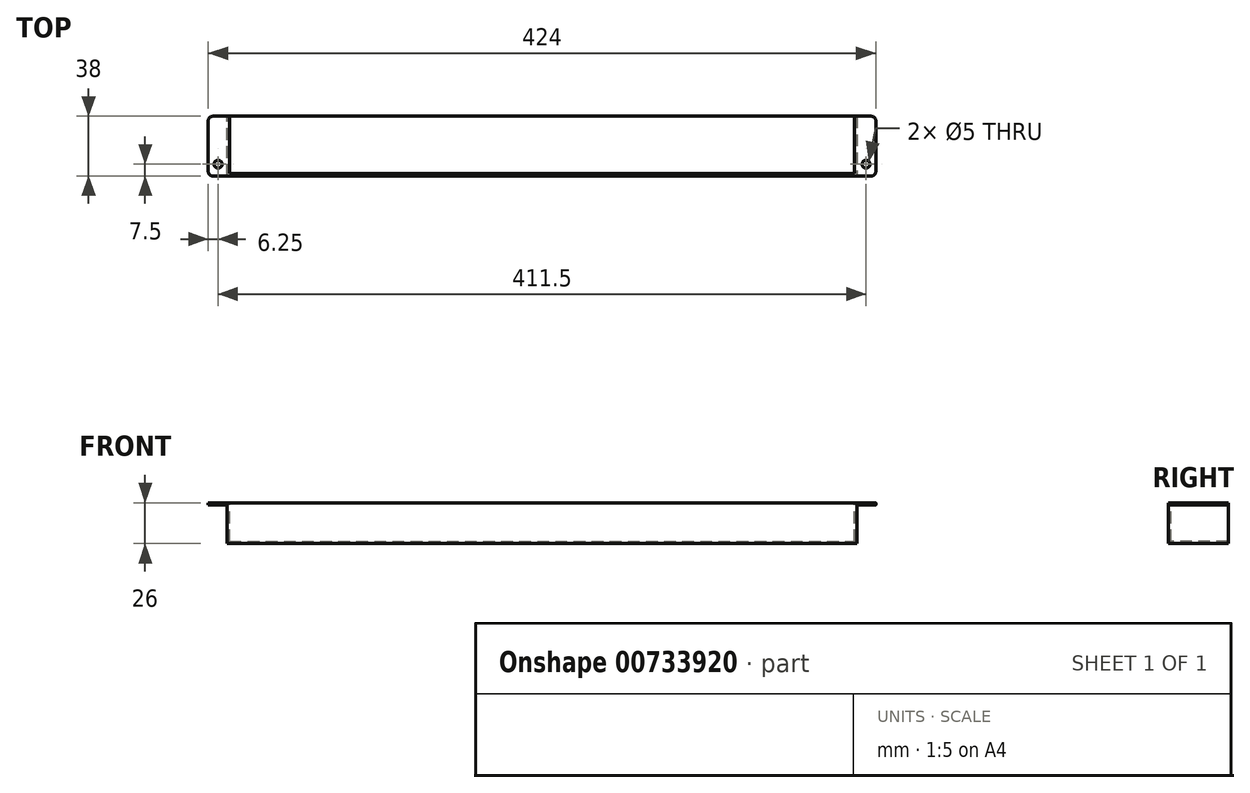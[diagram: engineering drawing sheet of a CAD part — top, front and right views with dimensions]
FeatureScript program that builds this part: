
annotation { "Feature Type Name" : "Feature", "Feature Type Description" : "" }
export const myFeature = defineFeature(function(context is Context, id is Id, definition is map)
    precondition{}
    {
        {
            var Q0;
            Q0=qCreatedBy(makeId("Front.planeOp"),FACE);
            var sketch = newSketch(context, id + "F0", { "sketchPlane" : qUnion([Q0])});
            skLineSegment(sketch, "E0.bottom", {"start": v(0, 0) * mm, "end": v(400, 0) * mm});
            skLineSegment(sketch, "E0.top", {"start": v(0, 26) * mm, "end": v(400, 26) * mm});
            skLineSegment(sketch, "E0.left", {"start": v(0, 0) * mm, "end": v(0, 26) * mm});
            skLineSegment(sketch, "E0.right", {"start": v(400, 0) * mm, "end": v(400, 26) * mm});
            skSolve(sketch);
        }
        {
            var Q0;
            Q0 = qSketchRegion(id + "F0", true);
            extrude(context, id + "F1", {"entities" : qUnion([Q0]), "oppositeDirection" : true, "depth" : 38 * mm, "offsetDistance" : 25 * mm});
        }
        {
            var Q0;
            Q0=makeQuery(id+"F1.opExtrude","SWEPT_FACE",FACE,{"disambiguationData":[OSD([sQuery(id+"F0.wireOp",EDGE,"E0.top")])]});
            var Q1;
            Q1=makeQuery(id+"F1.opExtrude","CAP_FACE",FACE,{"disambiguationData":[OSD([sQuery(id+"F0.wireOp",EDGE,"E0.bottom"),sQuery(id+"F0.wireOp",EDGE,"E0.top"),sQuery(id+"F0.wireOp",EDGE,"E0.left"),sQuery(id+"F0.wireOp",EDGE,"E0.right")])],"isStart":false});
            shell(context, id + "F2", {"entities" : qUnion([Q0, Q1]), "thickness" : 1.5 * mm});
        }
        {
            var Q0;
            Q0=makeQuery(id+"F1.opExtrude","SWEPT_FACE",FACE,{"disambiguationData":[OSD([sQuery(id+"F0.wireOp",EDGE,"E0.right")])]});
            var sketch = newSketch(context, id + "F3", { "sketchPlane" : qUnion([Q0])});
            skLineSegment(sketch, "E1.bottom", {"start": v(0, 26) * mm, "end": v(38, 26) * mm});
            skLineSegment(sketch, "E1.top", {"start": v(0, 24.5) * mm, "end": v(38, 24.5) * mm});
            skLineSegment(sketch, "E1.left", {"start": v(0, 26) * mm, "end": v(0, 24.5) * mm});
            skLineSegment(sketch, "E1.right", {"start": v(38, 26) * mm, "end": v(38, 24.5) * mm});
            skSolve(sketch);
        }
        {
            var Q0;
            Q0 = qSketchRegion(id + "F3", true);
            extrude(context, id + "F4", {"entities" : qUnion([Q0]), "operationType" : NewBodyOperationType.ADD, "depth" : 12 * mm, "offsetDistance" : 25 * mm});
        }
        {
            var Q0;
            Q0=makeQuery(id+"F1.opExtrude","SWEPT_FACE",FACE,{"disambiguationData":[OSD([sQuery(id+"F0.wireOp",EDGE,"E0.left")])]});
            var sketch = newSketch(context, id + "F5", { "sketchPlane" : qUnion([Q0])});
            skLineSegment(sketch, "E2.bottom", {"start": v(0, 26) * mm, "end": v(-38, 26) * mm});
            skLineSegment(sketch, "E2.top", {"start": v(0, 24.5) * mm, "end": v(-38, 24.5) * mm});
            skLineSegment(sketch, "E2.left", {"start": v(0, 26) * mm, "end": v(0, 24.5) * mm});
            skLineSegment(sketch, "E2.right", {"start": v(-38, 26) * mm, "end": v(-38, 24.5) * mm});
            skSolve(sketch);
        }
        {
            var Q0;
            Q0 = qSketchRegion(id + "F5", true);
            extrude(context, id + "F6", {"entities" : qUnion([Q0]), "operationType" : NewBodyOperationType.ADD, "depth" : 12 * mm, "offsetDistance" : 25 * mm});
        }
        {
            var Q0;
            Q0=makeQuery(id+"F6.boolean.opBoolean","MERGE",FACE,{"derivedFrom":[makeQuery(id+"F4.boolean.opBoolean","MERGE",FACE,{"derivedFrom":[makeQuery(id+"F1.opExtrude","SWEPT_FACE",FACE,{"disambiguationData":[OSD([sQuery(id+"F0.wireOp",EDGE,"E0.top")])]}),makeQuery(id+"F4.opExtrude","SWEPT_FACE",FACE,{"disambiguationData":[OSD([sQuery(id+"F3.wireOp",EDGE,"E1.bottom")])]})]}),makeQuery(id+"F6.opExtrude","SWEPT_FACE",FACE,{"disambiguationData":[OSD([sQuery(id+"F5.wireOp",EDGE,"E2.bottom")])]})]});
            var sketch = newSketch(context, id + "F7", { "sketchPlane" : qUnion([Q0])});
            skCircle(sketch, "E3", {"center": v(405.75, 7.5) * mm, "radius": 2.5 * mm});
            skCircle(sketch, "E4", {"center": v(-5.75, 7.5) * mm, "radius": 2.5 * mm});
            skSolve(sketch);
        }
        {
            var Q0;
            Q0 = qSketchRegion(id + "F7", true);
            extrude(context, id + "F8", {"entities" : qUnion([Q0]), "operationType" : NewBodyOperationType.REMOVE, "endBound" : BoundingType.UP_TO_NEXT, "oppositeDirection" : true, "depth" : 25 * mm, "offsetDistance" : 25 * mm});
        }
        {
            var Q0;
            Q0=makeQuery(id+"F6.opExtrude","CAP_EDGE",EDGE,{"disambiguationData":[OSD([sQuery(id+"F5.wireOp",EDGE,"E2.left")])],"isStart":false});
            var Q1;
            Q1=makeQuery(id+"F6.opExtrude","CAP_EDGE",EDGE,{"disambiguationData":[OSD([sQuery(id+"F5.wireOp",EDGE,"E2.right")])],"isStart":false});
            var Q2;
            Q2=makeQuery(id+"F4.opExtrude","CAP_EDGE",EDGE,{"disambiguationData":[OSD([sQuery(id+"F3.wireOp",EDGE,"E1.left")])],"isStart":false});
            var Q3;
            Q3=makeQuery(id+"F4.opExtrude","CAP_EDGE",EDGE,{"disambiguationData":[OSD([sQuery(id+"F3.wireOp",EDGE,"E1.right")])],"isStart":false});
            fillet(context, id + "F9", {"entities" : qUnion([Q0, Q1, Q2, Q3]), "radius" : 3 * mm, "tangentPropagation" : true, "allowEdgeOverflow" : false});
        }
    });
